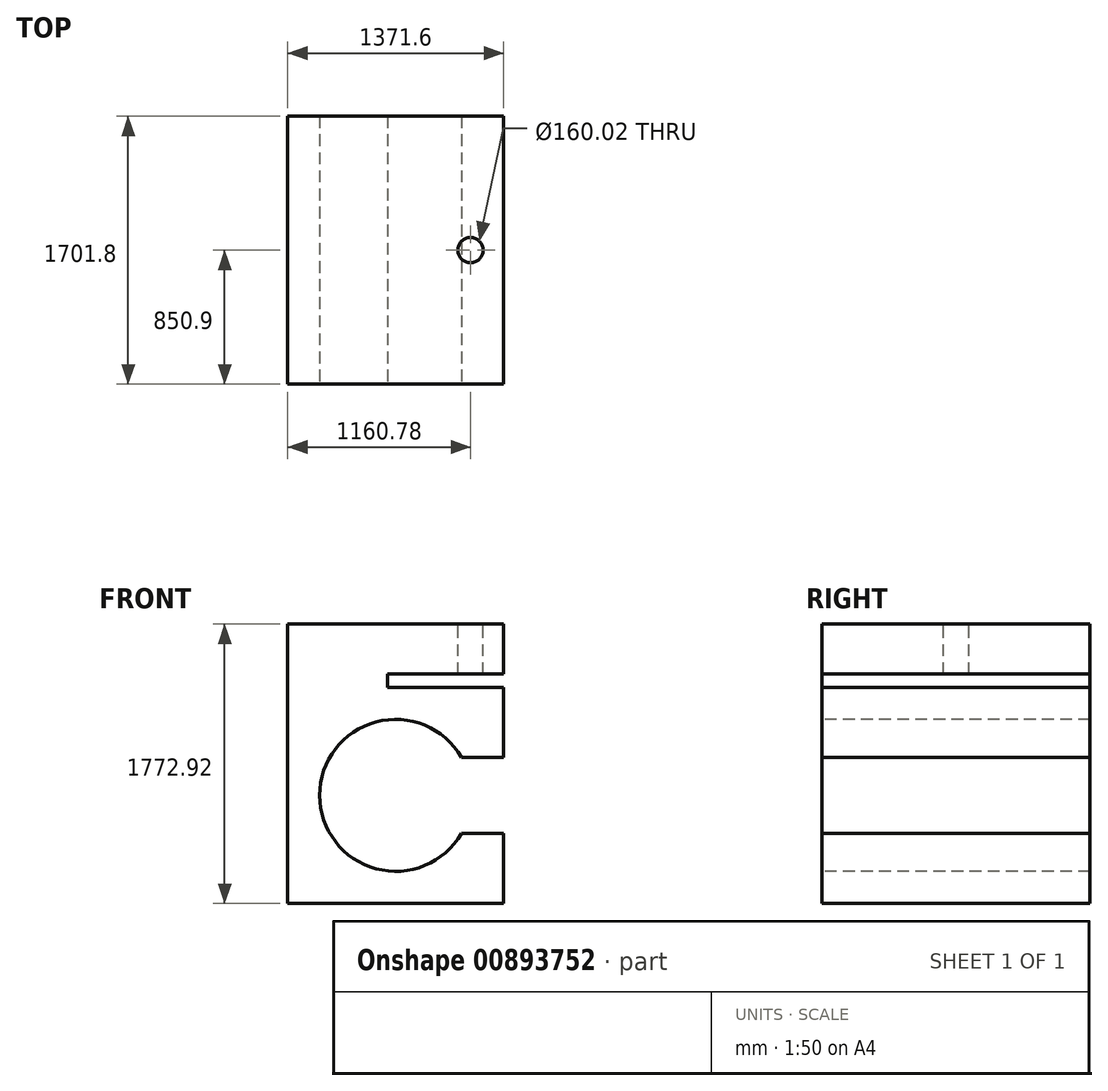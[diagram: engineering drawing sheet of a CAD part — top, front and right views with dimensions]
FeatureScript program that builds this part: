
annotation { "Feature Type Name" : "Feature", "Feature Type Description" : "" }
export const myFeature = defineFeature(function(context is Context, id is Id, definition is map)
    precondition{}
    {
        {
            var Q0;
            Q0=qCreatedBy(makeId("Front.planeOp"),FACE);
            var sketch = newSketch(context, id + "F0", { "sketchPlane" : qUnion([Q0])});
            skLineSegment(sketch, "E0.bottom", {"start": v(-44.6, -33.87) * mm, "end": v(1327, -33.87) * mm});
            skLineSegment(sketch, "E0.top", {"start": v(-44.6, 1739.05) * mm, "end": v(1327, 1739.05) * mm});
            skLineSegment(sketch, "E0.left", {"start": v(-44.6, -33.87) * mm, "end": v(-44.6, 1739.05) * mm});
            skLineSegment(sketch, "E0.right", {"start": v(1327, -33.87) * mm, "end": v(1327, 1739.05) * mm});
            skSolve(sketch);
        }
        {
            var Q0;
            Q0=qCreatedBy(makeId("Front.planeOp"),FACE);
            var sketch = newSketch(context, id + "F1", { "sketchPlane" : qUnion([Q0])});
            skSolve(sketch);
        }
        {
            var Q0;
            Q0 = qSketchRegion(id + "F1", true);
            var Q1;
            Q1=makeQuery(id+"F0.imprint","IMPRINT",FACE,{"disambiguationData":[TD([[makeQuery(id+"F0.imprint","IMPRINT",EDGE,{"derivedFrom":sQuery(id+"F0.wireOp",EDGE,"E0.bottom")}),1.0]])]});
            extrude(context, id + "F2", {"entities" : qUnion([Q0, Q1]), "depth" : 1701.8 * mm, "offsetDistance" : 25.4 * mm});
        }
        {
            var Q0;
            Q0=makeQuery(id+"F2.opExtrude","CAP_FACE",FACE,{"disambiguationData":[OSD([sQuery(id+"F0.wireOp",EDGE,"E0.bottom"),sQuery(id+"F0.wireOp",EDGE,"E0.top"),sQuery(id+"F0.wireOp",EDGE,"E0.left"),sQuery(id+"F0.wireOp",EDGE,"E0.right")])],"isStart":false});
            var sketch = newSketch(context, id + "F3", { "sketchPlane" : qUnion([Q0])});
            skLineSegment(sketch, "E1.bottom", {"start": v(1327, 1421.55) * mm, "end": v(590.4, 1421.55) * mm});
            skLineSegment(sketch, "E1.top", {"start": v(1327, 1337.73) * mm, "end": v(590.4, 1337.73) * mm});
            skLineSegment(sketch, "E1.left", {"start": v(1327, 1421.55) * mm, "end": v(1327, 1337.73) * mm});
            skLineSegment(sketch, "E1.right", {"start": v(590.4, 1421.55) * mm, "end": v(590.4, 1337.73) * mm});
            skSolve(sketch);
        }
        {
            var Q0;
            Q0 = qSketchRegion(id + "F3", true);
            extrude(context, id + "F4", {"entities" : qUnion([Q0]), "operationType" : NewBodyOperationType.REMOVE, "oppositeDirection" : true, "depth" : 1701.8 * mm, "offsetDistance" : 25.4 * mm});
        }
        {
            var Q0;
            Q0=makeQuery(id+"F2.opExtrude","CAP_FACE",FACE,{"disambiguationData":[OSD([sQuery(id+"F0.wireOp",EDGE,"E0.bottom"),sQuery(id+"F0.wireOp",EDGE,"E0.top"),sQuery(id+"F0.wireOp",EDGE,"E0.left"),sQuery(id+"F0.wireOp",EDGE,"E0.right")])],"isStart":false});
            var sketch = newSketch(context, id + "F5", { "sketchPlane" : qUnion([Q0])});
            skCircle(sketch, "E2", {"center": v(641.2, 651.93) * mm, "radius": 482.6 * mm});
            skLineSegment(sketch, "E3.bottom", {"start": v(1327, 893.23) * mm, "end": v(692, 893.23) * mm});
            skLineSegment(sketch, "E3.top", {"start": v(1327, 410.63) * mm, "end": v(692, 410.63) * mm});
            skLineSegment(sketch, "E3.left", {"start": v(1327, 893.23) * mm, "end": v(1327, 410.63) * mm});
            skLineSegment(sketch, "E3.right", {"start": v(692, 893.23) * mm, "end": v(692, 410.63) * mm});
            skSolve(sketch);
        }
        {
            var Q0;
            Q0 = qSketchRegion(id + "F5", true);
            extrude(context, id + "F6", {"entities" : qUnion([Q0]), "operationType" : NewBodyOperationType.REMOVE, "oppositeDirection" : true, "depth" : 1701.8 * mm, "offsetDistance" : 25.4 * mm});
        }
        {
            var Q0;
            Q0=makeQuery(id+"F2.opExtrude","SWEPT_FACE",FACE,{"disambiguationData":[OSD([sQuery(id+"F0.wireOp",EDGE,"E0.top")])]});
            var sketch = newSketch(context, id + "F7", { "sketchPlane" : qUnion([Q0])});
            skCircle(sketch, "E4", {"center": v(1116.18, -850.9) * mm, "radius": 80.01 * mm});
            skSolve(sketch);
        }
        {
            var Q0;
            Q0 = qSketchRegion(id + "F7", true);
            extrude(context, id + "F8", {"entities" : qUnion([Q0]), "operationType" : NewBodyOperationType.REMOVE, "oppositeDirection" : true, "depth" : 317.5 * mm, "offsetDistance" : 25.4 * mm});
        }
    });
